# Revit family: FP_Revit_18_HC36DTXB1_Rangehood_90000953A
name_source: partatom
category: Specialty Equipment
revit_build: Autodesk Revit 2018 (Build: 20170223_1515(x64)
units: mm (PartAtom-declared; Revit-internal decimal feet)

## family parameters
Always vertical = Yes
Cut with Voids When Loaded = Yes
OmniClass Number = 23.40.40.00
OmniClass Title = Food Service Equipment and Furnishings
Part Type = Normal
Room Calculation Point = No
Round Connector Dimension = Use Diameter
Shared = No
Work Plane-Based = No

## types (1)
- FP_Revit_18_HC36DTXB1_Rangehood_90000953A
    Chassis - Depth = 291 mm  [stored 0.954724 ft]
    Chassis - Height = 604 mm  [stored 1.98163 ft]
    Chassis - Width = 320 mm  [stored 1.04987 ft]
    Connector Description - Electrical = 120 V, 60 Hz, 542 W
    Connector Description - Extraction = 6” (152 mm) diameter, rigid or semi-rigid ducting, 615 CFM
    Description = 36" Rangehood
    Manufacturer = Fisher & Paykel Appliances
    Material - Body = Fisher & Paykel - Stainless Steel
    Material - Display Panel = Fisher & Paykel - Glass, Black
    Model = HC36DTXB1
    Product - Depth = 500 mm  [stored 1.64042 ft]
    Product - Width = 900 mm  [stored 2.95276 ft]
    URL = www.fisherpaykel.com

note: [stored X ft] marks values corroborated as IEEE doubles in the binary element streams (Revit-internal decimal feet)

## geometry (parser evidence)
native form markers: Sweep x5
no freeform markers — native parametric forms only
